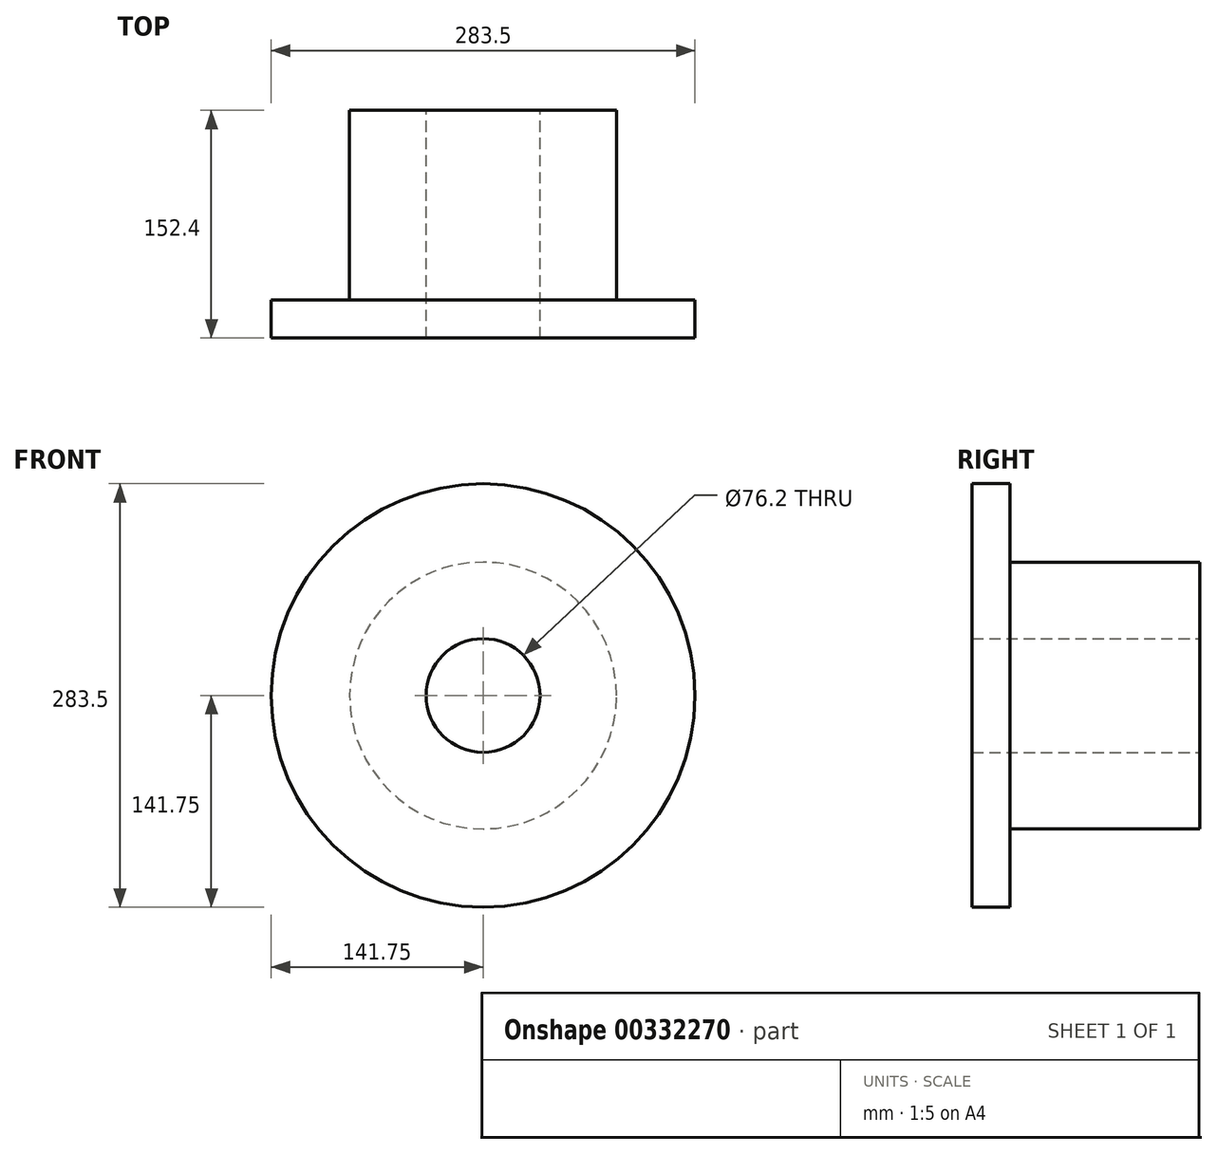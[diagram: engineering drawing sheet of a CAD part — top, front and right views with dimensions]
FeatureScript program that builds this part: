
annotation { "Feature Type Name" : "Feature", "Feature Type Description" : "" }
export const myFeature = defineFeature(function(context is Context, id is Id, definition is map)
    precondition{}
    {
        {
            var Q0;
            Q0=qCreatedBy(makeId("Front.planeOp"),FACE);
            var sketch = newSketch(context, id + "F0", { "sketchPlane" : qUnion([Q0])});
            skCircle(sketch, "E0", {"center": v(0, 0) * mm, "radius": 89.3 * mm});
            skSolve(sketch);
        }
        {
            var Q0;
            Q0 = qSketchRegion(id + "F0", true);
            extrude(context, id + "F1", {"entities" : qUnion([Q0]), "depth" : 127 * mm});
        }
        {
            var Q0;
            Q0=makeQuery(id+"F1.opExtrude","CAP_FACE",FACE,{"disambiguationData":[OSD([sQuery(id+"F0.wireOp",EDGE,"E0")])],"isStart":false});
            var sketch = newSketch(context, id + "F2", { "sketchPlane" : qUnion([Q0])});
            skCircle(sketch, "E1", {"center": v(0, 0) * mm, "radius": 141.75 * mm});
            skSolve(sketch);
        }
        {
            var Q0;
            Q0 = qSketchRegion(id + "F2", true);
            extrude(context, id + "F3", {"entities" : qUnion([Q0]), "operationType" : NewBodyOperationType.ADD, "depth" : 25.4 * mm});
        }
        {
            var Q0;
            Q0=makeQuery(id+"F1.opExtrude","CAP_FACE",FACE,{"disambiguationData":[OSD([sQuery(id+"F0.wireOp",EDGE,"E0")])],"isStart":true});
            var sketch = newSketch(context, id + "F4", { "sketchPlane" : qUnion([Q0])});
            skCircle(sketch, "E2", {"center": v(0, 0) * mm, "radius": 39.76 * mm});
            skSolve(sketch);
        }
        {
            var Q0;
            Q0=sQuery(id+"F4.wireOp",VERTEX,"E2.center");
            var Q1;
            Q1=makeQuery(id+"F1.opExtrude","SWEPT_BODY",BODY,{"disambiguationData":[OSD([sQuery(id+"F0.wireOp",EDGE,"E0")])]});
            hole(context, id + "F5", {"style" : HoleStyle.SIMPLE, "endStyle" : HoleEndStyle.THROUGH, "holeDiameter" : 76.2 * mm, "tappedDepth" : 12.7 * mm, "tapClearance" : 3, "locations" : qUnion([Q0]), "scope" : qUnion([Q1])});
        }
    });
